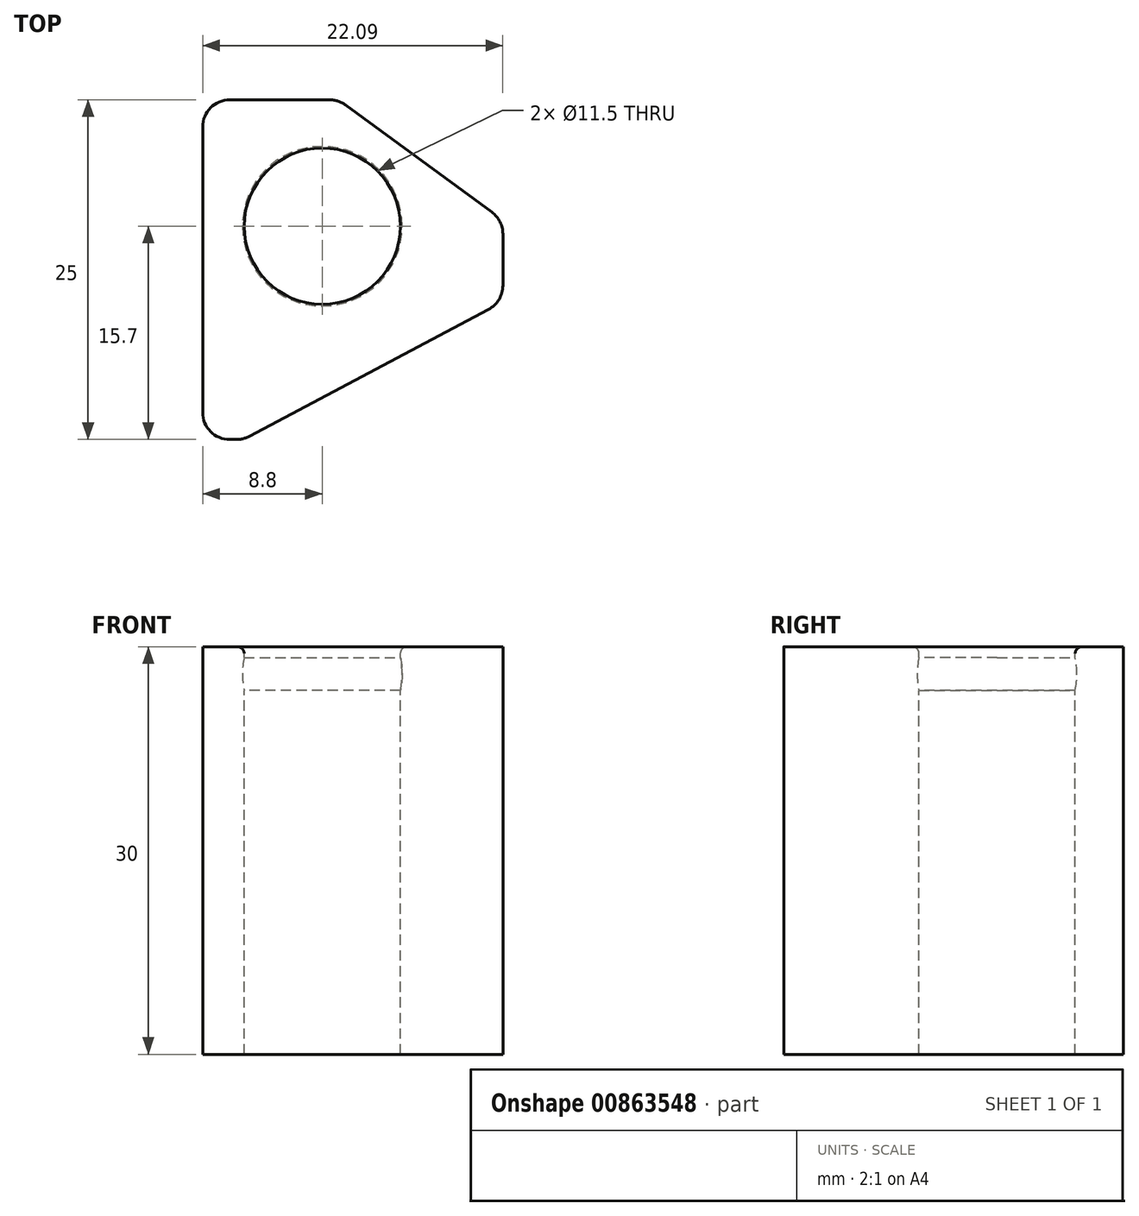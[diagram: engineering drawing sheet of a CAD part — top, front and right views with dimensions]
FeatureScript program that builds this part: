
annotation { "Feature Type Name" : "Feature", "Feature Type Description" : "" }
export const myFeature = defineFeature(function(context is Context, id is Id, definition is map)
    precondition{}
    {
        {
            var Q0;
            Q0=qCreatedBy(makeId("Top.planeOp"),FACE);
            var sketch = newSketch(context, id + "F0", { "sketchPlane" : qUnion([Q0])});
            skLineSegment(sketch, "E0", {"start": v(-8.8, -15.7) * mm, "end": v(-8.8, 9.3) * mm});
            skLineSegment(sketch, "E1", {"start": v(-8.8, 9.3) * mm, "end": v(1.2, 9.3) * mm});
            skLineSegment(sketch, "E2", {"start": v(-8.8, -15.7) * mm, "end": v(-5.8, -15.7) * mm});
            skLineSegment(sketch, "E3", {"start": v(1.2, 9.3) * mm, "end": v(13.3, 0.43) * mm});
            skPoint(sketch, "E4", {"position": v(-8.8, -15.7) * mm});
            skCircle(sketch, "E5", {"center": v(0, 0) * mm, "radius": 5.75 * mm});
            skLineSegment(sketch, "E6", {"start": v(13.3, 0.43) * mm, "end": v(13.3, -5.57) * mm});
            skLineSegment(sketch, "E7", {"start": v(13.3, -5.57) * mm, "end": v(-5.8, -15.7) * mm});
            skSolve(sketch);
        }
        {
            var Q0;
            Q0 = qSketchRegion(id + "F0", true);
            extrude(context, id + "F1", {"entities" : qUnion([Q0]), "oppositeDirection" : true, "depth" : 30 * mm, "offsetDistance" : 25 * mm});
        }
        {
            var Q0;
            Q0=makeQuery(id+"F1.opExtrude","SWEPT_EDGE",EDGE,{"disambiguationData":[OSD([sQuery(id+"F0.wireOp",EDGE,"E0"),sQuery(id+"F0.wireOp",EDGE,"E1")])]});
            var Q1;
            Q1=makeQuery(id+"F1.opExtrude","SWEPT_EDGE",EDGE,{"disambiguationData":[OSD([sQuery(id+"F0.wireOp",EDGE,"E1"),sQuery(id+"F0.wireOp",EDGE,"E3")])]});
            var Q2;
            Q2=makeQuery(id+"F1.opExtrude","SWEPT_EDGE",EDGE,{"disambiguationData":[OSD([sQuery(id+"F0.wireOp",EDGE,"E0"),sQuery(id+"F0.wireOp",EDGE,"E2")])]});
            var Q3;
            Q3=makeQuery(id+"F1.opExtrude","SWEPT_EDGE",EDGE,{"disambiguationData":[OSD([sQuery(id+"F0.wireOp",EDGE,"E2"),sQuery(id+"F0.wireOp",EDGE,"HqeiokMj-yoNG-ObOO-xvh2-qxyMi08B53wq")])]});
            var Q4;
            Q4=makeQuery(id+"F1.opExtrude","SWEPT_EDGE",EDGE,{"disambiguationData":[OSD([sQuery(id+"F0.wireOp",EDGE,"HqeiokMj-yoNG-ObOO-xvh2-qxyMi08B53wq"),sQuery(id+"F0.wireOp",EDGE,"E3")])]});
            var Q5;
            Q5=makeQuery(id+"F1.opExtrude","SWEPT_EDGE",EDGE,{"disambiguationData":[OSD([sQuery(id+"F0.wireOp",EDGE,"E6"),sQuery(id+"F0.wireOp",EDGE,"E7")])]});
            fillet(context, id + "F2", {"entities" : qUnion([Q0, Q1, Q2, Q3, Q4, Q5]), "tangentPropagation" : true, "radius" : 2 * mm, "defaultsChanged" : false, "vertexSettings" : [], "allowEdgeOverflow" : false});
        }
        {
            var Q0;
            Q0=qCreatedBy(makeId("Right.planeOp"),FACE);
            var sketch = newSketch(context, id + "F3", { "sketchPlane" : qUnion([Q0])});
            skLineSegment(sketch, "E8", {"start": v(0, 0) * mm, "end": v(0, -2) * mm, "construction": true});
            skCircle(sketch, "E9", {"center": v(0, -2) * mm, "radius": 5.88 * mm, "construction": true});
            skArc(sketch, "E10", {"start": v(-5.52, 0) * mm, "mid": v(-4.8, -5.37) * mm, "end": v(0, -7.88) * mm});
            skLineSegment(sketch, "E11", {"start": v(0, -7.88) * mm, "end": v(0, 0) * mm});
            skLineSegment(sketch, "E12", {"start": v(-5.52, 0) * mm, "end": v(0, 0) * mm});
            skSolve(sketch);
        }
        {
            var Q0;
            Q0=makeQuery(id+"F3.imprint","IMPRINT",FACE,{"disambiguationData":[TD([[makeQuery(id+"F3.imprint","IMPRINT",EDGE,{"derivedFrom":sQuery(id+"F3.wireOp",EDGE,"E10")}),1.0]])]});
            var Q1;
            Q1=sQuery(id+"F3.wireOp",EDGE,"E12");
            var Q2;
            Q2=sQuery(id+"F3.wireOp",EDGE,"E10");
            var Q3;
            Q3=sQuery(id+"F3.wireOp",EDGE,"E11");
            var Q4;
            Q4=sQuery(id+"F3.wireOp",EDGE,"E8");
            revolve(context, id + "F4", {"operationType" : NewBodyOperationType.REMOVE, "surfaceOperationType" : NewSurfaceOperationType.NEW, "entities" : qUnion([Q0]), "surfaceEntities" : qUnion([Q1, Q2, Q3]), "axis" : qUnion([Q4]), "revolveType" : RevolveType.FULL, "oppositeDirection" : true});
        }
        {
            var Q0;
            Q0=makeQuery(id+"F1.opExtrude","CAP_EDGE",EDGE,{"disambiguationData":[OSD([sQuery(id+"F0.wireOp",EDGE,"E5")])],"isStart":true});
            fillet(context, id + "F5", {"entities" : qUnion([Q0]), "radius" : 0.5 * mm, "defaultsChanged" : true, "vertexSettings" : [], "allowEdgeOverflow" : false});
        }
    });
